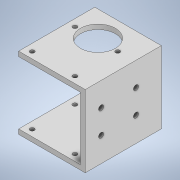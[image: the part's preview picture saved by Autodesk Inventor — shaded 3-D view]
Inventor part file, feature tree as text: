
AUTODESK INVENTOR PART (.ipt)
format: ipt  version: 2022 (Build 260153000, 153)  size: 167,936 bytes
history: native  units: mm
features: sketch x6, hole x4, extrude x2, other x1
ambient origin geometry x8: Origin, YZ Plane, XZ Plane, XY Plane, X Axis, Y Axis, Z Axis, Center Point
bodies: Body1 (feature_tree)
feature tree (13):
  other  "ソリッド1"
  extrude  "押し出し1"  Depth=48.0mm
  extrude  "押し出し2"  Depth=42.0mm
  hole  "穴1"  [1 undecoded]
  hole  "穴2"  [1 undecoded]
  hole  "穴3"  [1 undecoded]
  hole  "穴4"  [1 undecoded]
  sketch  "スケッチ1"
  sketch  "スケッチ2"
  sketch  "スケッチ3"
  sketch  "スケッチ4"
  sketch  "スケッチ5"
  sketch  "スケッチ6"
note: 4 required parameter values undecoded (feature->parameter linkage not recoverable at this tier; creation-order binding heuristic only, values carry confidence <= 0.55)
